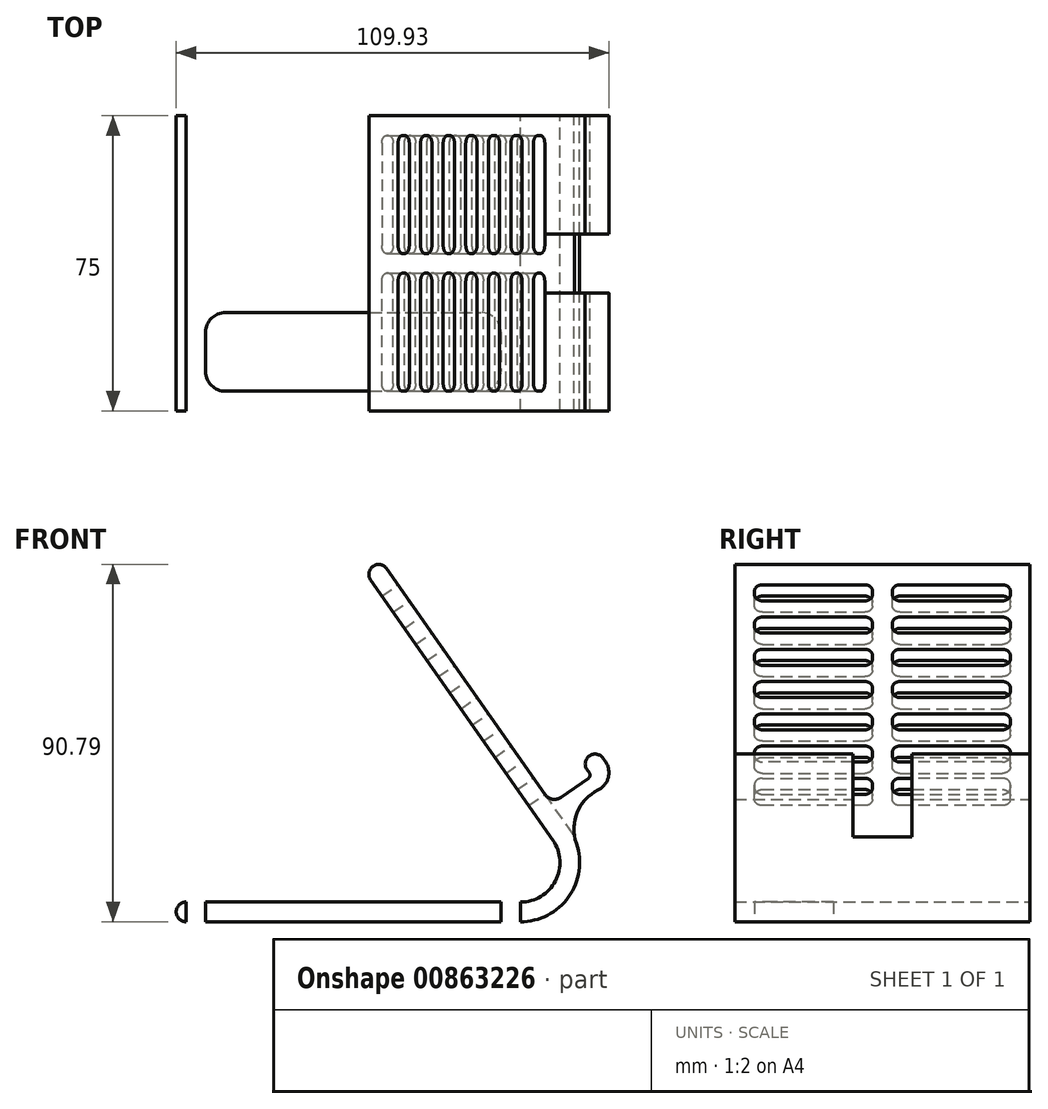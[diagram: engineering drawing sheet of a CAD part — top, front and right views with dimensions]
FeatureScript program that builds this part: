
annotation { "Feature Type Name" : "Feature", "Feature Type Description" : "" }
export const myFeature = defineFeature(function(context is Context, id is Id, definition is map)
    precondition{}
    {
        {
            assignVariable(context, id + "F0", {"name" : "baseWeight", "anyValue" : 75});
        }
        {
            var Q0;
            Q0=qCreatedBy(makeId("Front.planeOp"),FACE);
            var sketch = newSketch(context, id + "F1", { "sketchPlane" : qUnion([Q0])});
            skLineSegment(sketch, "E0", {"start": v(-70.37, 0) * mm, "end": v(14.63, 0) * mm});
            skLineSegment(sketch, "E1", {"start": v(22.82, 15.74) * mm, "end": v(-23.47, 81.85) * mm});
            skLineSegment(sketch, "E2.0", {"start": v(20.77, 27.38) * mm, "end": v(-19.38, 84.72) * mm});
            skLineSegment(sketch, "E2.2", {"start": v(-70.37, -5) * mm, "end": v(14.63, -5) * mm});
            skArc(sketch, "E3", {"start": v(-70.37, 0) * mm, "mid": v(-72.87, -2.5) * mm, "end": v(-70.37, -5) * mm});
            skArc(sketch, "E4", {"start": v(-23.47, 81.85) * mm, "mid": v(-22.86, 85.33) * mm, "end": v(-19.38, 84.72) * mm});
            skLineSegment(sketch, "E5", {"start": v(24.95, 26.64) * mm, "end": v(31.83, 31.46) * mm});
            skLineSegment(sketch, "E6", {"start": v(36.17, 35.72) * mm, "end": v(35.6, 36.54) * mm});
            skLineSegment(sketch, "E7.0", {"start": v(32.08, 32.85) * mm, "end": v(31.5, 33.67) * mm});
            skArc(sketch, "E8", {"start": v(31.5, 33.67) * mm, "mid": v(32.12, 37.15) * mm, "end": v(35.6, 36.54) * mm});
            skArc(sketch, "E9.filletArc", {"start": v(31.83, 31.46) * mm, "mid": v(32.24, 32.1) * mm, "end": v(32.08, 32.85) * mm});
            skPoint(sketch, "E10.visualSharp", {"position": v(22.5, 24.92) * mm});
            skArc(sketch, "E10.filletArc", {"start": v(20.77, 27.38) * mm, "mid": v(22.71, 26.15) * mm, "end": v(24.95, 26.64) * mm});
            skArc(sketch, "E11.filletArc", {"start": v(14.63, 0) * mm, "mid": v(23.5, 5.38) * mm, "end": v(22.82, 15.74) * mm});
            skLineSegment(sketch, "E12", {"start": v(31.5, 33.67) * mm, "end": v(41.07, 40.37) * mm, "construction": true});
            skArc(sketch, "E13.0", {"start": v(14.63, -5) * mm, "mid": v(26.86, 1.3) * mm, "end": v(28.8, 14.93) * mm});
            skArc(sketch, "E14", {"start": v(36.17, 35.72) * mm, "mid": v(36.91, 31.68) * mm, "end": v(34.33, 28.48) * mm});
            skArc(sketch, "E15", {"start": v(34.33, 28.48) * mm, "mid": v(29, 22.75) * mm, "end": v(28.8, 14.93) * mm});
            skSolve(sketch);
        }
        {
            var Q0;
            {var subQ0=sQuery(id+"F1.wireOp",EDGE,"E2.1");Q0=makeQuery(id+"F1.imprint","IMPRINT",FACE,{"disambiguationData":[TD([[makeQuery(id+"F1.imprint","IMPRINT",EDGE,{"derivedFrom":subQ0}),-1.0]])]});}
            var Q1;
            Q1=makeQuery(id+"F1.imprint","IMPRINT",FACE,{"disambiguationData":[TD([[makeQuery(id+"F1.imprint","IMPRINT",EDGE,{"derivedFrom":sQuery(id+"F1.wireOp",EDGE,"E0")}),-1.0]])]});
            var Q2;
            {var subQ0=sQuery(id+"F1.wireOp",EDGE,"E6");Q2=makeQuery(id+"F1.imprint","IMPRINT",FACE,{"disambiguationData":[TD([[makeQuery(id+"F1.imprint","IMPRINT",EDGE,{"derivedFrom":subQ0}),1.0]])]});}
            extrude(context, id + "F2", {"entities" : qUnion([Q0, Q1, Q2]), "depth" : (getVariable(context, 'baseWeight')) * mm, "offsetDistance" : 25 * mm});
        }
        {
            var Q0;
            Q0=makeQuery(id+"F2.opExtrude","SWEPT_FACE",FACE,{"disambiguationData":[OSD([sQuery(id+"F1.wireOp",EDGE,"E2.0")])]});
            var sketch = newSketch(context, id + "F3", { "sketchPlane" : qUnion([Q0])});
            skLineSegment(sketch, "E16.0", {"start": v(-75, 10.51) * mm, "end": v(0, 10.51) * mm});
            skLineSegment(sketch, "E17", {"start": v(-37.5, -35.2) * mm, "end": v(-37.5, 181.88) * mm, "construction": true});
            skLineSegment(sketch, "E18.bottom", {"start": v(-42, 75.51) * mm, "end": v(-68, 75.51) * mm});
            skLineSegment(sketch, "E18.top", {"start": v(-42, 70.51) * mm, "end": v(-68, 70.51) * mm});
            skLineSegment(sketch, "E18.left", {"start": v(-40, 73.51) * mm, "end": v(-40, 72.51) * mm});
            skLineSegment(sketch, "E18.right", {"start": v(-70, 73.51) * mm, "end": v(-70, 72.51) * mm});
            skLineSegment(sketch, "E19", {"start": v(-40, 75.51) * mm, "end": v(0, 75.51) * mm});
            skLineSegment(sketch, "E20", {"start": v(-40, 75.51) * mm, "end": v(-40, 80.51) * mm});
            skLineSegment(sketch, "E21", {"start": v(-70, 75.51) * mm, "end": v(-75, 75.51) * mm});
            skPoint(sketch, "E22.visualSharp", {"position": v(-70, 75.51) * mm});
            skArc(sketch, "E22.filletArc", {"start": v(-68, 75.51) * mm, "mid": v(-69.41, 74.93) * mm, "end": v(-70, 73.51) * mm});
            skPoint(sketch, "E23.visualSharp", {"position": v(-70, 70.51) * mm});
            skArc(sketch, "E23.filletArc", {"start": v(-70, 72.51) * mm, "mid": v(-69.41, 71.1) * mm, "end": v(-68, 70.51) * mm});
            skPoint(sketch, "E24.visualSharp", {"position": v(-40, 70.51) * mm});
            skArc(sketch, "E24.filletArc", {"start": v(-42, 70.51) * mm, "mid": v(-40.59, 71.1) * mm, "end": v(-40, 72.51) * mm});
            skPoint(sketch, "E25.visualSharp", {"position": v(-40, 75.51) * mm});
            skArc(sketch, "E25.filletArc", {"start": v(-40, 73.51) * mm, "mid": v(-40.59, 74.93) * mm, "end": v(-42, 75.51) * mm});
            skLineSegment(sketch, "E26.0.1.0", {"start": v(-42, 65.51) * mm, "end": v(-68, 65.51) * mm});
            skArc(sketch, "E26.0.1.1", {"start": v(-40, 63.51) * mm, "mid": v(-40.59, 64.93) * mm, "end": v(-42, 65.51) * mm});
            skLineSegment(sketch, "E26.0.1.2", {"start": v(-40, 63.51) * mm, "end": v(-40, 62.51) * mm});
            skArc(sketch, "E26.0.1.3", {"start": v(-42, 60.51) * mm, "mid": v(-40.59, 61.1) * mm, "end": v(-40, 62.51) * mm});
            skLineSegment(sketch, "E26.0.1.4", {"start": v(-42, 60.51) * mm, "end": v(-68, 60.51) * mm});
            skArc(sketch, "E26.0.1.5", {"start": v(-70, 62.51) * mm, "mid": v(-69.41, 61.1) * mm, "end": v(-68, 60.51) * mm});
            skLineSegment(sketch, "E26.0.1.6", {"start": v(-70, 63.51) * mm, "end": v(-70, 62.51) * mm});
            skArc(sketch, "E26.0.1.7", {"start": v(-68, 65.51) * mm, "mid": v(-69.41, 64.93) * mm, "end": v(-70, 63.51) * mm});
            skLineSegment(sketch, "E26.direction1", {"start": v(-68, 75.51) * mm, "end": v(-33, 75.51) * mm, "construction": true});
            skLineSegment(sketch, "E26.direction2", {"start": v(-68, 75.51) * mm, "end": v(-68, 65.51) * mm, "construction": true});
            skLineSegment(sketch, "E27.0.0.2", {"start": v(-42, 55.51) * mm, "end": v(-68, 55.51) * mm});
            skArc(sketch, "E27.3.0.2", {"start": v(-40, 53.51) * mm, "mid": v(-40.59, 54.93) * mm, "end": v(-42, 55.51) * mm});
            skLineSegment(sketch, "E27.7.0.2", {"start": v(-40, 53.51) * mm, "end": v(-40, 52.51) * mm});
            skArc(sketch, "E27.10.0.2", {"start": v(-42, 50.51) * mm, "mid": v(-40.59, 51.1) * mm, "end": v(-40, 52.51) * mm});
            skLineSegment(sketch, "E27.14.0.2", {"start": v(-42, 50.51) * mm, "end": v(-68, 50.51) * mm});
            skArc(sketch, "E27.17.0.2", {"start": v(-70, 52.51) * mm, "mid": v(-69.41, 51.1) * mm, "end": v(-68, 50.51) * mm});
            skLineSegment(sketch, "E27.21.0.2", {"start": v(-70, 53.51) * mm, "end": v(-70, 52.51) * mm});
            skArc(sketch, "E27.24.0.2", {"start": v(-68, 55.51) * mm, "mid": v(-69.41, 54.93) * mm, "end": v(-70, 53.51) * mm});
            skLineSegment(sketch, "E27.0.0.3", {"start": v(-42, 45.51) * mm, "end": v(-68, 45.51) * mm});
            skArc(sketch, "E27.3.0.3", {"start": v(-40, 43.51) * mm, "mid": v(-40.59, 44.93) * mm, "end": v(-42, 45.51) * mm});
            skLineSegment(sketch, "E27.7.0.3", {"start": v(-40, 43.51) * mm, "end": v(-40, 42.51) * mm});
            skArc(sketch, "E27.10.0.3", {"start": v(-42, 40.51) * mm, "mid": v(-40.59, 41.1) * mm, "end": v(-40, 42.51) * mm});
            skLineSegment(sketch, "E27.14.0.3", {"start": v(-42, 40.51) * mm, "end": v(-68, 40.51) * mm});
            skArc(sketch, "E27.17.0.3", {"start": v(-70, 42.51) * mm, "mid": v(-69.41, 41.1) * mm, "end": v(-68, 40.51) * mm});
            skLineSegment(sketch, "E27.21.0.3", {"start": v(-70, 43.51) * mm, "end": v(-70, 42.51) * mm});
            skArc(sketch, "E27.24.0.3", {"start": v(-68, 45.51) * mm, "mid": v(-69.41, 44.93) * mm, "end": v(-70, 43.51) * mm});
            skLineSegment(sketch, "E27.0.0.4", {"start": v(-42, 35.51) * mm, "end": v(-68, 35.51) * mm});
            skArc(sketch, "E27.3.0.4", {"start": v(-40, 33.51) * mm, "mid": v(-40.59, 34.93) * mm, "end": v(-42, 35.51) * mm});
            skLineSegment(sketch, "E27.7.0.4", {"start": v(-40, 33.51) * mm, "end": v(-40, 32.51) * mm});
            skArc(sketch, "E27.10.0.4", {"start": v(-42, 30.51) * mm, "mid": v(-40.59, 31.1) * mm, "end": v(-40, 32.51) * mm});
            skLineSegment(sketch, "E27.14.0.4", {"start": v(-42, 30.51) * mm, "end": v(-68, 30.51) * mm});
            skArc(sketch, "E27.17.0.4", {"start": v(-70, 32.51) * mm, "mid": v(-69.41, 31.1) * mm, "end": v(-68, 30.51) * mm});
            skLineSegment(sketch, "E27.21.0.4", {"start": v(-70, 33.51) * mm, "end": v(-70, 32.51) * mm});
            skArc(sketch, "E27.24.0.4", {"start": v(-68, 35.51) * mm, "mid": v(-69.41, 34.93) * mm, "end": v(-70, 33.51) * mm});
            skLineSegment(sketch, "E28.0.1.0", {"start": v(-7, 75.51) * mm, "end": v(-33, 75.51) * mm});
            skArc(sketch, "E28.3.1.0", {"start": v(-5, 73.51) * mm, "mid": v(-5.59, 74.93) * mm, "end": v(-7, 75.51) * mm});
            skLineSegment(sketch, "E28.7.1.0", {"start": v(-5, 73.51) * mm, "end": v(-5, 72.51) * mm});
            skArc(sketch, "E28.10.1.0", {"start": v(-7, 70.51) * mm, "mid": v(-5.59, 71.1) * mm, "end": v(-5, 72.51) * mm});
            skLineSegment(sketch, "E28.14.1.0", {"start": v(-7, 70.51) * mm, "end": v(-33, 70.51) * mm});
            skArc(sketch, "E28.17.1.0", {"start": v(-35, 72.51) * mm, "mid": v(-34.41, 71.1) * mm, "end": v(-33, 70.51) * mm});
            skLineSegment(sketch, "E28.21.1.0", {"start": v(-35, 73.51) * mm, "end": v(-35, 72.51) * mm});
            skArc(sketch, "E28.24.1.0", {"start": v(-33, 75.51) * mm, "mid": v(-34.41, 74.93) * mm, "end": v(-35, 73.51) * mm});
            skLineSegment(sketch, "E28.0.1.1", {"start": v(-7, 65.51) * mm, "end": v(-33, 65.51) * mm});
            skArc(sketch, "E28.3.1.1", {"start": v(-5, 63.51) * mm, "mid": v(-5.59, 64.93) * mm, "end": v(-7, 65.51) * mm});
            skLineSegment(sketch, "E28.7.1.1", {"start": v(-5, 63.51) * mm, "end": v(-5, 62.51) * mm});
            skArc(sketch, "E28.10.1.1", {"start": v(-7, 60.51) * mm, "mid": v(-5.59, 61.1) * mm, "end": v(-5, 62.51) * mm});
            skLineSegment(sketch, "E28.14.1.1", {"start": v(-7, 60.51) * mm, "end": v(-33, 60.51) * mm});
            skArc(sketch, "E28.17.1.1", {"start": v(-35, 62.51) * mm, "mid": v(-34.41, 61.1) * mm, "end": v(-33, 60.51) * mm});
            skLineSegment(sketch, "E28.21.1.1", {"start": v(-35, 63.51) * mm, "end": v(-35, 62.51) * mm});
            skArc(sketch, "E28.24.1.1", {"start": v(-33, 65.51) * mm, "mid": v(-34.41, 64.93) * mm, "end": v(-35, 63.51) * mm});
            skLineSegment(sketch, "E28.0.1.2", {"start": v(-7, 55.51) * mm, "end": v(-33, 55.51) * mm});
            skArc(sketch, "E28.3.1.2", {"start": v(-5, 53.51) * mm, "mid": v(-5.59, 54.93) * mm, "end": v(-7, 55.51) * mm});
            skLineSegment(sketch, "E28.7.1.2", {"start": v(-5, 53.51) * mm, "end": v(-5, 52.51) * mm});
            skArc(sketch, "E28.10.1.2", {"start": v(-7, 50.51) * mm, "mid": v(-5.59, 51.1) * mm, "end": v(-5, 52.51) * mm});
            skLineSegment(sketch, "E28.14.1.2", {"start": v(-7, 50.51) * mm, "end": v(-33, 50.51) * mm});
            skArc(sketch, "E28.17.1.2", {"start": v(-35, 52.51) * mm, "mid": v(-34.41, 51.1) * mm, "end": v(-33, 50.51) * mm});
            skLineSegment(sketch, "E28.21.1.2", {"start": v(-35, 53.51) * mm, "end": v(-35, 52.51) * mm});
            skArc(sketch, "E28.24.1.2", {"start": v(-33, 55.51) * mm, "mid": v(-34.41, 54.93) * mm, "end": v(-35, 53.51) * mm});
            skLineSegment(sketch, "E28.0.1.3", {"start": v(-7, 45.51) * mm, "end": v(-33, 45.51) * mm});
            skArc(sketch, "E28.3.1.3", {"start": v(-5, 43.51) * mm, "mid": v(-5.59, 44.93) * mm, "end": v(-7, 45.51) * mm});
            skLineSegment(sketch, "E28.7.1.3", {"start": v(-5, 43.51) * mm, "end": v(-5, 42.51) * mm});
            skArc(sketch, "E28.10.1.3", {"start": v(-7, 40.51) * mm, "mid": v(-5.59, 41.1) * mm, "end": v(-5, 42.51) * mm});
            skLineSegment(sketch, "E28.14.1.3", {"start": v(-7, 40.51) * mm, "end": v(-33, 40.51) * mm});
            skArc(sketch, "E28.17.1.3", {"start": v(-35, 42.51) * mm, "mid": v(-34.41, 41.1) * mm, "end": v(-33, 40.51) * mm});
            skLineSegment(sketch, "E28.21.1.3", {"start": v(-35, 43.51) * mm, "end": v(-35, 42.51) * mm});
            skArc(sketch, "E28.24.1.3", {"start": v(-33, 45.51) * mm, "mid": v(-34.41, 44.93) * mm, "end": v(-35, 43.51) * mm});
            skLineSegment(sketch, "E28.0.1.4", {"start": v(-7, 35.51) * mm, "end": v(-33, 35.51) * mm});
            skArc(sketch, "E28.3.1.4", {"start": v(-5, 33.51) * mm, "mid": v(-5.59, 34.93) * mm, "end": v(-7, 35.51) * mm});
            skLineSegment(sketch, "E28.7.1.4", {"start": v(-5, 33.51) * mm, "end": v(-5, 32.51) * mm});
            skArc(sketch, "E28.10.1.4", {"start": v(-7, 30.51) * mm, "mid": v(-5.59, 31.1) * mm, "end": v(-5, 32.51) * mm});
            skLineSegment(sketch, "E28.14.1.4", {"start": v(-7, 30.51) * mm, "end": v(-33, 30.51) * mm});
            skArc(sketch, "E28.17.1.4", {"start": v(-35, 32.51) * mm, "mid": v(-34.41, 31.1) * mm, "end": v(-33, 30.51) * mm});
            skLineSegment(sketch, "E28.21.1.4", {"start": v(-35, 33.51) * mm, "end": v(-35, 32.51) * mm});
            skArc(sketch, "E28.24.1.4", {"start": v(-33, 35.51) * mm, "mid": v(-34.41, 34.93) * mm, "end": v(-35, 33.51) * mm});
            skLineSegment(sketch, "E29.0.0.5", {"start": v(-42, 25.51) * mm, "end": v(-68, 25.51) * mm});
            skArc(sketch, "E29.3.0.5", {"start": v(-40, 23.51) * mm, "mid": v(-40.59, 24.93) * mm, "end": v(-42, 25.51) * mm});
            skLineSegment(sketch, "E29.7.0.5", {"start": v(-40, 23.51) * mm, "end": v(-40, 22.51) * mm});
            skArc(sketch, "E29.10.0.5", {"start": v(-42, 20.51) * mm, "mid": v(-40.59, 21.1) * mm, "end": v(-40, 22.51) * mm});
            skLineSegment(sketch, "E29.14.0.5", {"start": v(-42, 20.51) * mm, "end": v(-68, 20.51) * mm});
            skArc(sketch, "E29.17.0.5", {"start": v(-70, 22.51) * mm, "mid": v(-69.41, 21.1) * mm, "end": v(-68, 20.51) * mm});
            skLineSegment(sketch, "E29.21.0.5", {"start": v(-70, 23.51) * mm, "end": v(-70, 22.51) * mm});
            skArc(sketch, "E29.24.0.5", {"start": v(-68, 25.51) * mm, "mid": v(-69.41, 24.93) * mm, "end": v(-70, 23.51) * mm});
            skLineSegment(sketch, "E29.0.0.6", {"start": v(-42, 15.51) * mm, "end": v(-68, 15.51) * mm});
            skArc(sketch, "E29.3.0.6", {"start": v(-40, 13.51) * mm, "mid": v(-40.59, 14.93) * mm, "end": v(-42, 15.51) * mm});
            skLineSegment(sketch, "E29.7.0.6", {"start": v(-40, 13.51) * mm, "end": v(-40, 12.51) * mm});
            skArc(sketch, "E29.10.0.6", {"start": v(-42, 10.51) * mm, "mid": v(-40.59, 11.1) * mm, "end": v(-40, 12.51) * mm});
            skLineSegment(sketch, "E29.14.0.6", {"start": v(-42, 10.51) * mm, "end": v(-68, 10.51) * mm});
            skArc(sketch, "E29.17.0.6", {"start": v(-70, 12.51) * mm, "mid": v(-69.41, 11.1) * mm, "end": v(-68, 10.51) * mm});
            skLineSegment(sketch, "E29.21.0.6", {"start": v(-70, 13.51) * mm, "end": v(-70, 12.51) * mm});
            skArc(sketch, "E29.24.0.6", {"start": v(-68, 15.51) * mm, "mid": v(-69.41, 14.93) * mm, "end": v(-70, 13.51) * mm});
            skLineSegment(sketch, "E29.0.1.5", {"start": v(-7, 25.51) * mm, "end": v(-33, 25.51) * mm});
            skArc(sketch, "E29.3.1.5", {"start": v(-5, 23.51) * mm, "mid": v(-5.59, 24.93) * mm, "end": v(-7, 25.51) * mm});
            skLineSegment(sketch, "E29.7.1.5", {"start": v(-5, 23.51) * mm, "end": v(-5, 22.51) * mm});
            skArc(sketch, "E29.10.1.5", {"start": v(-7, 20.51) * mm, "mid": v(-5.59, 21.1) * mm, "end": v(-5, 22.51) * mm});
            skLineSegment(sketch, "E29.14.1.5", {"start": v(-7, 20.51) * mm, "end": v(-33, 20.51) * mm});
            skArc(sketch, "E29.17.1.5", {"start": v(-35, 22.51) * mm, "mid": v(-34.41, 21.1) * mm, "end": v(-33, 20.51) * mm});
            skLineSegment(sketch, "E29.21.1.5", {"start": v(-35, 23.51) * mm, "end": v(-35, 22.51) * mm});
            skArc(sketch, "E29.24.1.5", {"start": v(-33, 25.51) * mm, "mid": v(-34.41, 24.93) * mm, "end": v(-35, 23.51) * mm});
            skLineSegment(sketch, "E29.0.1.6", {"start": v(-7, 15.51) * mm, "end": v(-33, 15.51) * mm});
            skArc(sketch, "E29.3.1.6", {"start": v(-5, 13.51) * mm, "mid": v(-5.59, 14.93) * mm, "end": v(-7, 15.51) * mm});
            skLineSegment(sketch, "E29.7.1.6", {"start": v(-5, 13.51) * mm, "end": v(-5, 12.51) * mm});
            skArc(sketch, "E29.10.1.6", {"start": v(-7, 10.51) * mm, "mid": v(-5.59, 11.1) * mm, "end": v(-5, 12.51) * mm});
            skLineSegment(sketch, "E29.14.1.6", {"start": v(-7, 10.51) * mm, "end": v(-33, 10.51) * mm});
            skArc(sketch, "E29.17.1.6", {"start": v(-35, 12.51) * mm, "mid": v(-34.41, 11.1) * mm, "end": v(-33, 10.51) * mm});
            skLineSegment(sketch, "E29.21.1.6", {"start": v(-35, 13.51) * mm, "end": v(-35, 12.51) * mm});
            skArc(sketch, "E29.24.1.6", {"start": v(-33, 15.51) * mm, "mid": v(-34.41, 14.93) * mm, "end": v(-35, 13.51) * mm});
            skSolve(sketch);
        }
        {
            var Q0;
            Q0 = qSketchRegion(id + "F3", true);
            extrude(context, id + "F4", {"entities" : qUnion([Q0]), "operationType" : NewBodyOperationType.REMOVE, "oppositeDirection" : true, "depth" : 25 * mm, "offsetDistance" : 25 * mm});
        }
        {
            var Q0;
            Q0=makeQuery(id+"F2.opExtrude","SWEPT_FACE",FACE,{"disambiguationData":[OSD([sQuery(id+"F1.wireOp",EDGE,"E6")])]});
            var sketch = newSketch(context, id + "F5", { "sketchPlane" : qUnion([Q0])});
            skLineSegment(sketch, "E30.bottom", {"start": v(-45, 16.9) * mm, "end": v(-30, 16.9) * mm});
            skLineSegment(sketch, "E30.top", {"start": v(-45, -2.88) * mm, "end": v(-30, -2.88) * mm});
            skLineSegment(sketch, "E30.left", {"start": v(-45, 16.9) * mm, "end": v(-45, -2.88) * mm});
            skLineSegment(sketch, "E30.right", {"start": v(-30, 16.9) * mm, "end": v(-30, -2.88) * mm});
            skSolve(sketch);
        }
        {
            var Q0;
            Q0 = qSketchRegion(id + "F5", true);
            extrude(context, id + "F6", {"entities" : qUnion([Q0]), "operationType" : NewBodyOperationType.REMOVE, "oppositeDirection" : true, "depth" : 17.4 * mm, "offsetDistance" : 25 * mm});
        }
        {
            var Q0;
            Q0=makeQuery(id+"F2.opExtrude","SWEPT_FACE",FACE,{"disambiguationData":[OSD([sQuery(id+"F1.wireOp",EDGE,"E2.2")])]});
            var Q1;
            Q1=makeQuery(id+"F2.opExtrude","SWEPT_FACE",FACE,{"disambiguationData":[OSD([sQuery(id+"F1.wireOp",EDGE,"E2.2")])]});
            var sketch = newSketch(context, id + "F7", { "sketchPlane" : qUnion([Q0, Q1])});
            skLineSegment(sketch, "E31.bottom", {"start": v(-60.37, 25) * mm, "end": v(4.63, 25) * mm});
            skLineSegment(sketch, "E31.top", {"start": v(-60.37, 5) * mm, "end": v(4.63, 5) * mm});
            skLineSegment(sketch, "E31.left", {"start": v(-65.37, 20) * mm, "end": v(-65.37, 10) * mm});
            skLineSegment(sketch, "E31.right", {"start": v(9.63, 20) * mm, "end": v(9.63, 10) * mm});
            skPoint(sketch, "E32.visualSharp", {"position": v(-65.37, 5) * mm});
            skArc(sketch, "E32.filletArc", {"start": v(-65.37, 10) * mm, "mid": v(-63.9, 6.46) * mm, "end": v(-60.37, 5) * mm});
            skPoint(sketch, "E33.visualSharp", {"position": v(-65.37, 25) * mm});
            skArc(sketch, "E33.filletArc", {"start": v(-60.37, 25) * mm, "mid": v(-63.9, 23.54) * mm, "end": v(-65.37, 20) * mm});
            skPoint(sketch, "E34.visualSharp", {"position": v(9.63, 25) * mm});
            skArc(sketch, "E34.filletArc", {"start": v(9.63, 20) * mm, "mid": v(8.17, 23.54) * mm, "end": v(4.63, 25) * mm});
            skPoint(sketch, "E35.visualSharp", {"position": v(9.63, 5) * mm});
            skArc(sketch, "E35.filletArc", {"start": v(4.63, 5) * mm, "mid": v(8.17, 6.46) * mm, "end": v(9.63, 10) * mm});
            skLineSegment(sketch, "E36", {"start": v(14.63, 37.5) * mm, "end": v(-70.37, 37.5) * mm, "construction": true});
            skArc(sketch, "E37.MirrorCS", {"start": v(-60.37, 50) * mm, "mid": v(-63.9, 51.46) * mm, "end": v(-65.37, 55) * mm});
            skLineSegment(sketch, "E38.MirrorCS", {"start": v(-60.37, 50) * mm, "end": v(4.63, 50) * mm});
            skArc(sketch, "E39.MirrorCS", {"start": v(9.63, 55) * mm, "mid": v(8.17, 51.46) * mm, "end": v(4.63, 50) * mm});
            skLineSegment(sketch, "E40.MirrorCS", {"start": v(9.63, 55) * mm, "end": v(9.63, 65) * mm});
            skArc(sketch, "E41.MirrorCS", {"start": v(4.63, 70) * mm, "mid": v(8.17, 68.54) * mm, "end": v(9.63, 65) * mm});
            skLineSegment(sketch, "E42.MirrorCS", {"start": v(-60.37, 70) * mm, "end": v(4.63, 70) * mm});
            skArc(sketch, "E43.MirrorCS", {"start": v(-65.37, 65) * mm, "mid": v(-63.9, 68.54) * mm, "end": v(-60.37, 70) * mm});
            skLineSegment(sketch, "E44.MirrorCS", {"start": v(-65.37, 55) * mm, "end": v(-65.37, 65) * mm});
            skSolve(sketch);
        }
        {
            var Q0;
            Q0=makeQuery(id+"F7.imprint","IMPRINT",FACE,{"disambiguationData":[TD([[makeQuery(id+"F7.imprint","IMPRINT",EDGE,{"derivedFrom":sQuery(id+"F7.wireOp",EDGE,"E31.bottom")}),-1.0]])]});
            var Q1;
            Q1=makeQuery(id+"F7.imprint","IMPRINT",FACE,{"disambiguationData":[TD([[makeQuery(id+"F7.imprint","IMPRINT",EDGE,{"derivedFrom":sQuery(id+"F7.wireOp",EDGE,"E37.MirrorCS")}),-1.0]])]});
            extrude(context, id + "F8", {"entities" : qUnion([Q0, Q1]), "operationType" : NewBodyOperationType.REMOVE, "oppositeDirection" : true, "depth" : 5 * mm, "offsetDistance" : 25 * mm});
        }
    });
